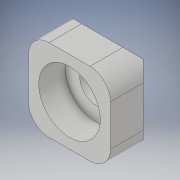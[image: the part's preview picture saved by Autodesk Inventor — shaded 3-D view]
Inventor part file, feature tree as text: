
AUTODESK INVENTOR PART (.ipt)
format: ipt  version: 2017 SP1 (Build 210196100, 196)  size: 131,072 bytes
history: native  units: in
note: dims shown in document units (in); Inventor stores cm internally (conversion verified against a paired STEP export)
features: sketch x2, extrude x1, hole x1, chamfer x1, fillet x1
ambient origin geometry x8: Origin, YZ Plane, XZ Plane, XY Plane, X Axis, Y Axis, Z Axis, Center Point
bodies: Solid1 (feature_tree)
feature tree (6):
  extrude  "Extrusion1"  Depth=0.5in
  hole  "Hole1"  [1 undecoded]
  chamfer  "Chamfer1"  Distance=0.125in
  fillet  "Fillet1"  [1 undecoded]
  sketch  "Sketch1"  dims[d0=0.5in d1=0.5in]
  sketch  "Sketch2"  dims[d2=0.25in d3=0.0in d4=0.2in d5=0.75in d6=0.375in d7=0.1625in d8=0.5635in d9=1.0in d10=0.8108in d11=0.05in d12=0.125in d13=45.0deg d14=0.125in]
note: 2 required parameter values undecoded (feature->parameter linkage not recoverable at this tier; creation-order binding heuristic only, values carry confidence <= 0.55)
